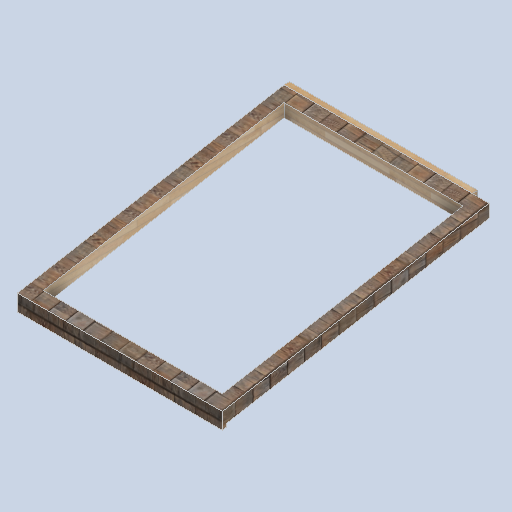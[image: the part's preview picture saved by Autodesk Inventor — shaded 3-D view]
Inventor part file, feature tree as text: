
AUTODESK INVENTOR PART (.ipt)
format: ipt  version: 2024.2 (Build 282272000, 272)  size: 414,720 bytes
history: native  units: mm
features: sketch x8, plane x5, extrude x4, projected_geometry x3, loft x1, other x1
ambient origin geometry x8: Origin, YZ Plane, XZ Plane, XY Plane, X Axis, Y Axis, Z Axis, Center Point
bodies: Solid1 (feature_tree)
feature tree (22):
  sketch  "Sketch2"  dims[d0=150.0mm d1=0.0mm d2=2500.0mm]
  plane  "Work Plane2"
  sketch  "Sketch3"  dims[d3=51.0mm d4=0.0mm d5=13.962634mm]
  extrude  "Extrusion1"  Depth=2500.0mm TaperAngle=0.0deg
  plane  "Work Plane3"
  sketch  "Sketch4"  dims[d6=13.962634mm d7=0.0mm d8=90.0deg]
  plane  "Work Plane4"
  sketch  "Sketch5"  dims[d9=0.0mm d10=90.0deg d11=36.0mm]
  loft  "Loft1"
  extrude  "Extrusion2"  TaperAngle=0.0deg  [1 undecoded]
  plane  "Work Plane5"
  extrude  "Extrusion3"  Depth=36.0mm
  extrude  "Extrusion4"  Depth=13.962634mm
  plane  "Work Plane1"
  projected_geometry  "Projected Loop1"
  sketch  "Sketch6"  dims[d12=30.0mm d13=13.962634mm]
  other  "Edges1"
  sketch  "Sketch7"  dims[d14=0.0mm d15=0.0mm]
  sketch  "Sketch8"  dims[d16=120.0mm]
  projected_geometry  "Projected Loop2"
  sketch  "Sketch9"  dims[d17=120.0mm d18=120.0mm d19=120.0mm d20=0.0mm d21=0.0mm d22=155.0mm d23=0.0mm d24=0.0mm]
  projected_geometry  "Projected Loop3"
note: 1 required parameter value undecoded (feature->parameter linkage not recoverable at this tier; creation-order binding heuristic only, values carry confidence <= 0.55)
